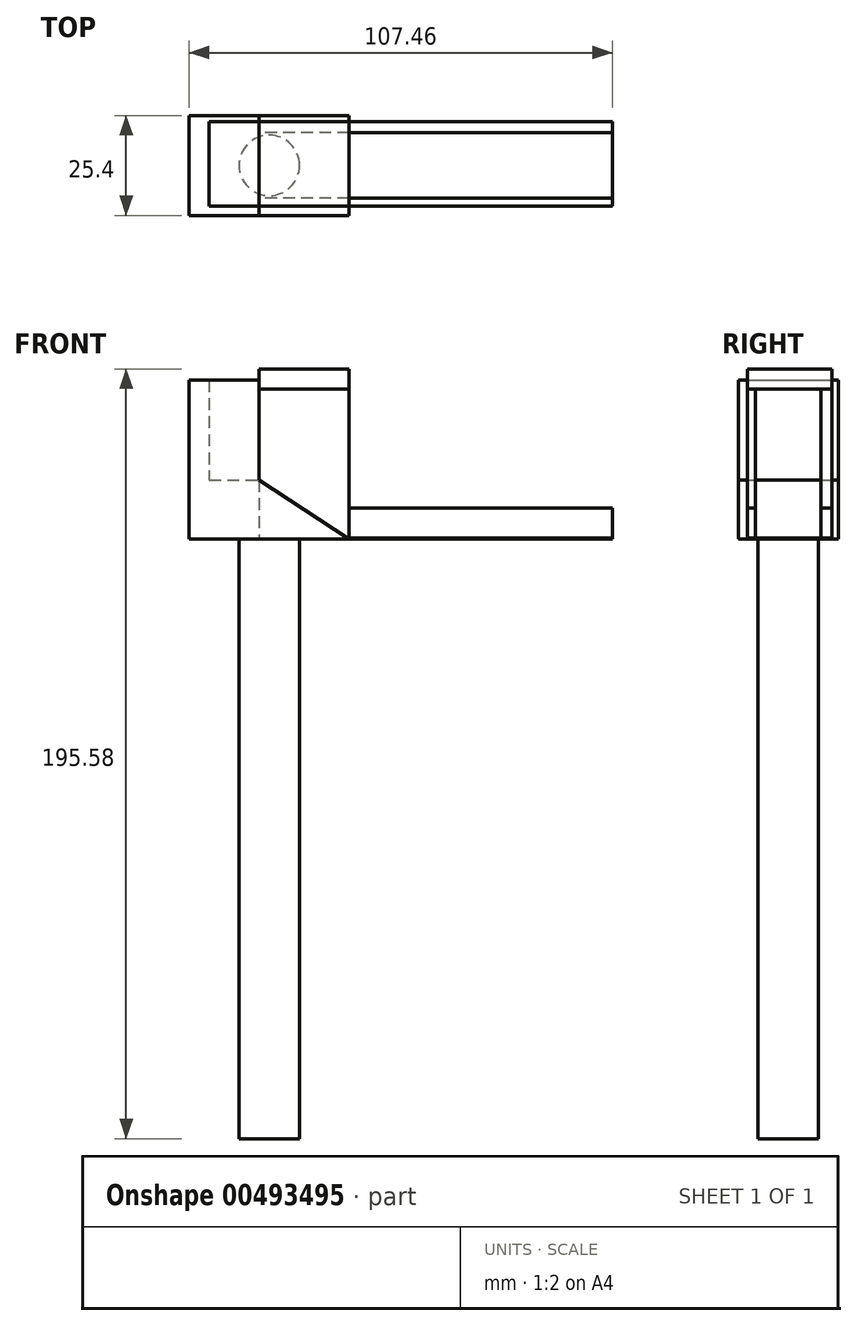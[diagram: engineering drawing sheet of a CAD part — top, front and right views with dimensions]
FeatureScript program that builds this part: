
annotation { "Feature Type Name" : "Feature", "Feature Type Description" : "" }
export const myFeature = defineFeature(function(context is Context, id is Id, definition is map)
    precondition{}
    {
        {
            var Q0;
            Q0=qCreatedBy(makeId("Front.planeOp"),FACE);
            var sketch = newSketch(context, id + "F0", { "sketchPlane" : qUnion([Q0])});
            skLineSegment(sketch, "E0", {"start": v(-42.59, 0) * mm, "end": v(-65.45, 14.93) * mm});
            skLineSegment(sketch, "E1", {"start": v(-65.45, 14.93) * mm, "end": v(-65.45, 0) * mm});
            skLineSegment(sketch, "E2", {"start": v(-65.45, 0) * mm, "end": v(-42.59, 0) * mm});
            skSolve(sketch);
        }
        {
            var Q0;
            Q0 = qSketchRegion(id + "F0", true);
            extrude(context, id + "F1", {"entities" : qUnion([Q0]), "endBound" : BoundingType.SYMMETRIC, "depth" : 25.4 * mm});
        }
        {
            var Q0;
            Q0=qCreatedBy(makeId("Front.planeOp"),FACE);
            var sketch = newSketch(context, id + "F2", { "sketchPlane" : qUnion([Q0])});
            skLineSegment(sketch, "E3.0", {"start": v(-65.45, 14.93) * mm, "end": v(-65.45, 0) * mm});
            skLineSegment(sketch, "E4", {"start": v(-65.45, 0) * mm, "end": v(-83.23, 0) * mm});
            skLineSegment(sketch, "E5", {"start": v(-83.23, 0) * mm, "end": v(-83.23, 14.93) * mm});
            skLineSegment(sketch, "E6", {"start": v(-83.23, 14.93) * mm, "end": v(-65.45, 14.93) * mm});
            skSolve(sketch);
        }
        {
            var Q0;
            Q0 = qSketchRegion(id + "F2", true);
            extrude(context, id + "F3", {"entities" : qUnion([Q0]), "operationType" : NewBodyOperationType.ADD, "endBound" : BoundingType.SYMMETRIC, "depth" : 25.4 * mm});
        }
        {
            var Q0;
            Q0=makeQuery(id+"F3.opExtrude","SWEPT_FACE",FACE,{"disambiguationData":[OSD([sQuery(id+"F2.wireOp",EDGE,"E6")])]});
            var sketch = newSketch(context, id + "F4", { "sketchPlane" : qUnion([Q0])});
            skLineSegment(sketch, "E7", {"start": v(-65.45, -12.7) * mm, "end": v(-65.45, -10.34) * mm});
            skLineSegment(sketch, "E8", {"start": v(-65.45, -10.34) * mm, "end": v(-78.15, -10.34) * mm});
            skLineSegment(sketch, "E9", {"start": v(-78.15, -10.34) * mm, "end": v(-78.15, 11.1) * mm});
            skLineSegment(sketch, "E10", {"start": v(-78.15, 11.1) * mm, "end": v(-65.45, 11.1) * mm});
            skLineSegment(sketch, "E11", {"start": v(-65.45, 11.1) * mm, "end": v(-65.45, 12.7) * mm});
            skSolve(sketch);
        }
        {
            var Q0;
            Q0 = qSketchRegion(id + "F4", true);
            var Q1;
            Q1=makeQuery(id+"F4.imprint","IMPRINT",FACE,{"disambiguationData":[TD([[makeQuery(id+"F4.imprint","IMPRINT",EDGE,{"derivedFrom":sQuery(id+"F4.wireOp",EDGE,"E7")}),1.0]])]});
            extrude(context, id + "F5", {"entities" : qUnion([Q0, Q1]), "operationType" : NewBodyOperationType.ADD, "depth" : 25.4 * mm});
        }
        {
            var Q0;
            Q0=qCreatedBy(makeId("Top.planeOp"),FACE);
            var sketch = newSketch(context, id + "F6", { "sketchPlane" : qUnion([Q0])});
            skLineSegment(sketch, "E12.0", {"start": v(-42.59, -12.7) * mm, "end": v(-42.59, 12.7) * mm});
            skLineSegment(sketch, "E13.0", {"start": v(-65.45, -10.34) * mm, "end": v(-65.45, 11.1) * mm});
            skPoint(sketch, "E14.0", {"position": v(-65.45, -10.34) * mm});
            skPoint(sketch, "E15.0", {"position": v(-65.45, 11.1) * mm});
            skLineSegment(sketch, "E16", {"start": v(-65.45, -10.34) * mm, "end": v(-42.59, -10.34) * mm});
            skLineSegment(sketch, "E17", {"start": v(-42.59, -10.34) * mm, "end": v(24.23, -10.34) * mm});
            skLineSegment(sketch, "E18", {"start": v(-65.45, 11.1) * mm, "end": v(24.23, 11.1) * mm});
            skLineSegment(sketch, "E19", {"start": v(24.23, 11.1) * mm, "end": v(24.23, -10.34) * mm});
            skLineSegment(sketch, "E20", {"start": v(-42.59, -10.34) * mm, "end": v(-42.59, -8.35) * mm});
            skLineSegment(sketch, "E21", {"start": v(-42.59, -8.35) * mm, "end": v(-62.36, -8.35) * mm});
            skLineSegment(sketch, "E22", {"start": v(-62.36, -8.35) * mm, "end": v(-65.45, -8.35) * mm});
            skLineSegment(sketch, "E23", {"start": v(-65.45, -8.35) * mm, "end": v(-65.45, -10.34) * mm});
            skLineSegment(sketch, "E24", {"start": v(-42.59, 12.7) * mm, "end": v(-42.59, 8.3) * mm});
            skLineSegment(sketch, "E25", {"start": v(-42.59, 8.3) * mm, "end": v(-65.45, 8.3) * mm});
            skSolve(sketch);
        }
        {
            var Q0;
            {var subQ0=sQuery(id+"F6.wireOp",EDGE,"E17");Q0=makeQuery(id+"F6.imprint","IMPRINT",FACE,{"disambiguationData":[TD([[makeQuery(id+"F6.imprint","IMPRINT",EDGE,{"derivedFrom":subQ0}),1.0]])]});}
            extrude(context, id + "F7", {"entities" : qUnion([Q0]), "depth" : 0.25 * mm});
        }
        {
            var Q0;
            {var subQ3=sQuery(id+"F6.wireOp",EDGE,"E25");Q0=makeQuery(id+"F6.imprint","IMPRINT",FACE,{"disambiguationData":[TD([[makeQuery(id+"F6.imprint","IMPRINT",EDGE,{"derivedFrom":subQ3}),-1.0]])]});}
            var Q1;
            Q1=makeQuery(id+"F6.imprint","IMPRINT",FACE,{"disambiguationData":[TD([[makeQuery(id+"F6.imprint","IMPRINT",EDGE,{"derivedFrom":sQuery(id+"F6.wireOp",EDGE,"E16")}),1.0]])]});
            extrude(context, id + "F8", {"entities" : qUnion([Q0, Q1]), "depth" : 38.1 * mm, "offsetDistance" : 25.4 * mm});
        }
        {
            var Q0;
            Q0=makeQuery(id+"F8.opExtrude","CAP_FACE",FACE,{"disambiguationData":[OSD([sQuery(id+"F6.wireOp",EDGE,"E13.0"),sQuery(id+"F6.wireOp",EDGE,"E18"),sQuery(id+"F6.wireOp",EDGE,"E24"),sQuery(id+"F6.wireOp",EDGE,"E25")])],"isStart":false});
            var sketch = newSketch(context, id + "F9", { "sketchPlane" : qUnion([Q0])});
            skLineSegment(sketch, "E26.0", {"start": v(-65.45, -10.34) * mm, "end": v(-42.59, -10.34) * mm});
            skLineSegment(sketch, "E27.0", {"start": v(-65.45, 11.1) * mm, "end": v(-42.59, 11.1) * mm});
            skLineSegment(sketch, "E28", {"start": v(-42.59, 11.1) * mm, "end": v(-42.59, -10.34) * mm});
            skLineSegment(sketch, "E29", {"start": v(-65.45, -10.34) * mm, "end": v(-65.45, 11.1) * mm});
            skSolve(sketch);
        }
        {
            var Q0;
            Q0 = qSketchRegion(id + "F9", true);
            extrude(context, id + "F10", {"entities" : qUnion([Q0]), "depth" : 5.08 * mm, "offsetDistance" : 25.4 * mm});
        }
        {
            var Q0;
            Q0=makeQuery(id+"F7.opExtrude","CAP_FACE",FACE,{"disambiguationData":[OSD([sQuery(id+"F6.wireOp",EDGE,"E12.0"),sQuery(id+"F6.wireOp",EDGE,"E17"),sQuery(id+"F6.wireOp",EDGE,"E18"),sQuery(id+"F6.wireOp",EDGE,"E19"),sQuery(id+"F6.wireOp",EDGE,"E20"),sQuery(id+"F6.wireOp",EDGE,"E24")])],"isStart":false});
            var sketch = newSketch(context, id + "F11", { "sketchPlane" : qUnion([Q0])});
            skPoint(sketch, "E30.0", {"position": v(-42.59, -10.34) * mm});
            skPoint(sketch, "E31.0", {"position": v(-42.59, -8.35) * mm});
            skPoint(sketch, "E32.0", {"position": v(-42.59, 8.3) * mm});
            skLineSegment(sketch, "E33", {"start": v(-42.59, 8.3) * mm, "end": v(24.23, 8.3) * mm});
            skLineSegment(sketch, "E34", {"start": v(-42.59, -8.35) * mm, "end": v(24.23, -8.35) * mm});
            skSolve(sketch);
        }
        {
            var Q0;
            {var subQ0=sQuery(id+"F11.wireOp",EDGE,"E34");Q0=makeQuery(id+"F11.imprint","IMPRINT",FACE,{"disambiguationData":[TD([[makeQuery(id+"F11.imprint","IMPRINT",EDGE,{"derivedFrom":subQ0}),-1.0]])]});}
            var Q1;
            {var subQ0=sQuery(id+"F11.wireOp",EDGE,"E33");Q1=makeQuery(id+"F11.imprint","IMPRINT",FACE,{"disambiguationData":[TD([[makeQuery(id+"F11.imprint","IMPRINT",EDGE,{"derivedFrom":subQ0}),1.0]])]});}
            extrude(context, id + "F12", {"entities" : qUnion([Q0, Q1]), "depth" : 7.62 * mm});
        }
        {
            var Q0;
            Q0=makeQuery(id+"F3.boolean.opBoolean","MERGE",FACE,{"derivedFrom":[makeQuery(id+"F1.opExtrude","SWEPT_FACE",FACE,{"disambiguationData":[OSD([sQuery(id+"F0.wireOp",EDGE,"E2")])]}),makeQuery(id+"F3.opExtrude","SWEPT_FACE",FACE,{"disambiguationData":[OSD([sQuery(id+"F2.wireOp",EDGE,"E4")])]})]});
            var sketch = newSketch(context, id + "F13", { "sketchPlane" : qUnion([Q0])});
            skLineSegment(sketch, "E35.0.0", {"start": v(-83.23, -12.7) * mm, "end": v(-42.59, -12.7) * mm});
            skLineSegment(sketch, "E35.0.1", {"start": v(-42.59, -12.7) * mm, "end": v(-42.59, 12.7) * mm});
            skLineSegment(sketch, "E35.0.2", {"start": v(-42.59, 12.7) * mm, "end": v(-83.23, 12.7) * mm});
            skLineSegment(sketch, "E35.0.3", {"start": v(-83.23, 12.7) * mm, "end": v(-83.23, -12.7) * mm});
            skLineSegment(sketch, "E36", {"start": v(-42.59, 0) * mm, "end": v(-83.23, 0) * mm});
            skCircle(sketch, "E37", {"center": v(-62.9, 0) * mm, "radius": 7.69 * mm});
            skSolve(sketch);
        }
        {
            var Q0;
            {var subQ0=sQuery(id+"F13.wireOp",EDGE,"E37");var subQ1=sQuery(id+"F13.wireOp",EDGE,"E36");var subQ2=makeQuery(id+"F13.imprint","INTERSECT",VERTEX,{"disambiguationData":[OD(0.0)],"derivedFrom":[subQ1,subQ0]});Q0=makeQuery(id+"F13.imprint","IMPRINT",FACE,{"disambiguationData":[TD([[makeQuery(id+"F13.imprint","IMPRINT",EDGE,{"disambiguationData":[TD([[subQ2,-1.0]])],"derivedFrom":subQ1}),-1.0]])]});}
            var Q1;
            {var subQ0=sQuery(id+"F13.wireOp",EDGE,"E37");var subQ1=sQuery(id+"F13.wireOp",EDGE,"E36");var subQ2=makeQuery(id+"F13.imprint","INTERSECT",VERTEX,{"disambiguationData":[OD(0.0)],"derivedFrom":[subQ1,subQ0]});Q1=makeQuery(id+"F13.imprint","IMPRINT",FACE,{"disambiguationData":[TD([[makeQuery(id+"F13.imprint","IMPRINT",EDGE,{"disambiguationData":[TD([[subQ2,-1.0]])],"derivedFrom":subQ1}),1.0]])]});}
            extrude(context, id + "F14", {"entities" : qUnion([Q0, Q1]), "operationType" : NewBodyOperationType.ADD, "depth" : 152.4 * mm});
        }
    });
